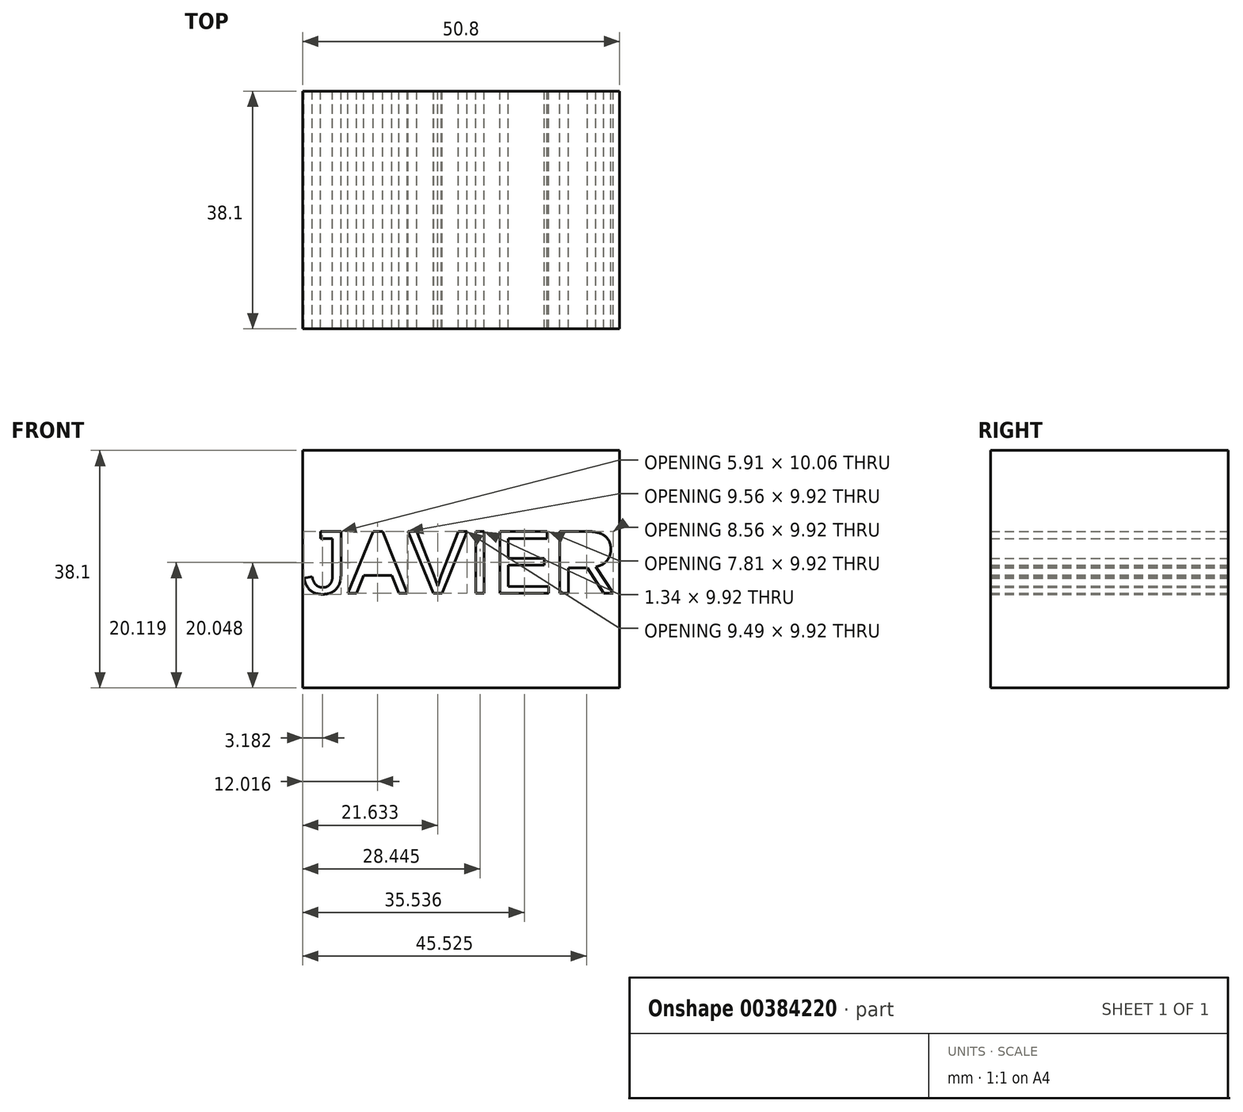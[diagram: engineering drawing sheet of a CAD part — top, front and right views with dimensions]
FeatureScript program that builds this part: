
annotation { "Feature Type Name" : "Feature", "Feature Type Description" : "" }
export const myFeature = defineFeature(function(context is Context, id is Id, definition is map)
    precondition{}
    {
        {
            var Q0;
            Q0=qCreatedBy(makeId("Front.planeOp"),FACE);
            var sketch = newSketch(context, id + "F0", { "sketchPlane" : qUnion([Q0])});
            skLineSegment(sketch, "E0.bottom", {"start": v(-61.48, 66.52) * mm, "end": v(-10.68, 66.52) * mm});
            skLineSegment(sketch, "E0.top", {"start": v(-61.48, 28.42) * mm, "end": v(-10.68, 28.42) * mm});
            skLineSegment(sketch, "E0.left", {"start": v(-61.48, 66.52) * mm, "end": v(-61.48, 28.42) * mm});
            skLineSegment(sketch, "E0.right", {"start": v(-10.68, 66.52) * mm, "end": v(-10.68, 28.42) * mm});
            skText(sketch, "E1", { "text": "JAVIER", "fontName": "Arimo-Regular.ttf"});
            const initialGuessF0  = {"E1": [-0.06148, 0.04358, 1, 0, 0.01038]};
            skSetInitialGuess(sketch, initialGuessF0);
            skSolve(sketch);
        }
        {
            var Q0;
            Q0 = qSketchRegion(id + "F0", true);
            extrude(context, id + "F1", {"entities" : qUnion([Q0]), "endBound" : BoundingType.SYMMETRIC, "depth" : 25.4 * mm});
        }
        {
            var Q0;
            Q0 = qSketchRegion(id + "F0", true);
            extrude(context, id + "F2", {"entities" : qUnion([Q0]), "operationType" : NewBodyOperationType.ADD, "depth" : 25.4 * mm});
        }
    });
